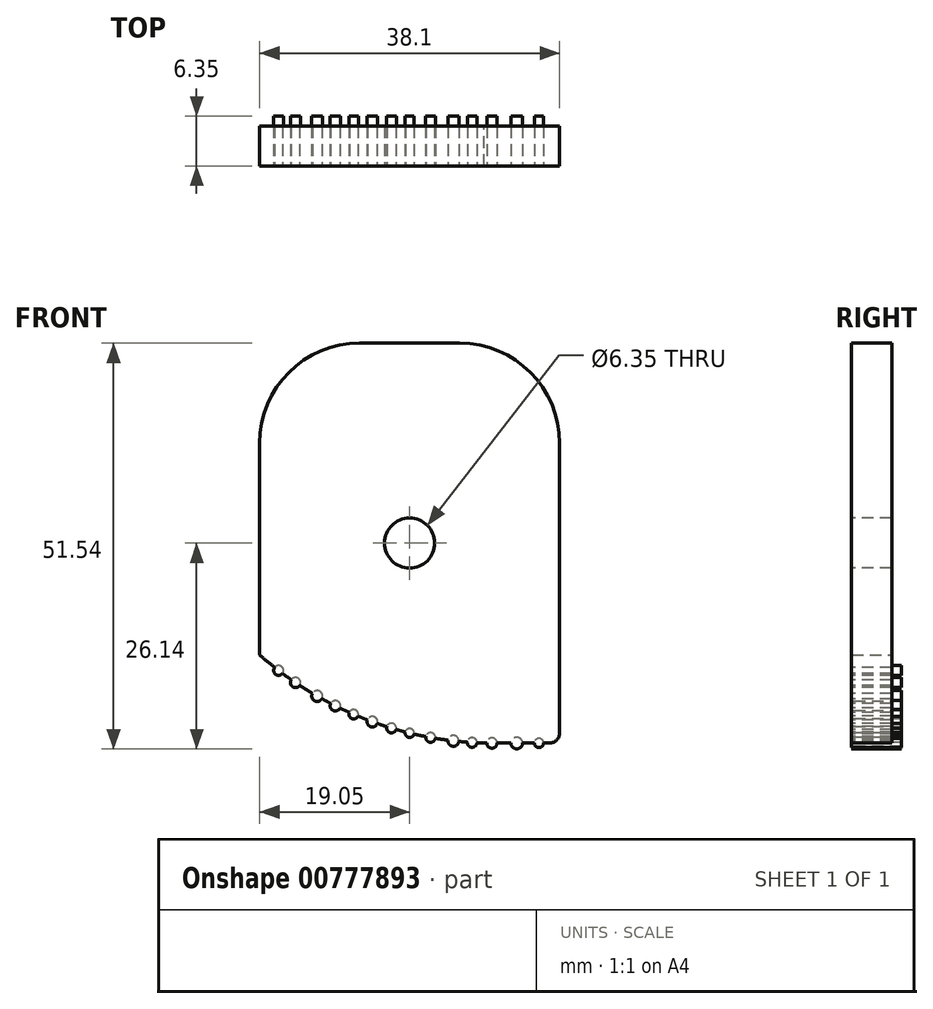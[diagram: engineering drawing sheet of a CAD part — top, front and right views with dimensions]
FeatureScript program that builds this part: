
annotation { "Feature Type Name" : "Feature", "Feature Type Description" : "" }
export const myFeature = defineFeature(function(context is Context, id is Id, definition is map)
    precondition{}
    {
        {
            var Q0;
            Q0=qCreatedBy(makeId("Front.planeOp"),FACE);
            var sketch = newSketch(context, id + "F0", { "sketchPlane" : qUnion([Q0])});
            skLineSegment(sketch, "E0.bottom", {"start": v(19.05, 25.4) * mm, "end": v(-19.05, 25.4) * mm});
            skLineSegment(sketch, "E0.top", {"start": v(19.05, -25.4) * mm, "end": v(-19.05, -25.4) * mm});
            skLineSegment(sketch, "E0.left", {"start": v(19.05, 25.4) * mm, "end": v(19.05, -25.4) * mm});
            skLineSegment(sketch, "E0.right", {"start": v(-19.05, 25.4) * mm, "end": v(-19.05, -25.4) * mm});
            skPoint(sketch, "E0.middle", {"position": v(0, 0) * mm});
            skArc(sketch, "E1", {"start": v(-19.05, -14.22) * mm, "mid": v(-5.78, -22.3) * mm, "end": v(9.44, -25.4) * mm});
            skSolve(sketch);
        }
        {
            var Q0;
            {var subQ1=sQuery(id+"F0.wireOp",EDGE,"E0.bottom");Q0=makeQuery(id+"F0.imprint","IMPRINT",FACE,{"disambiguationData":[TD([[makeQuery(id+"F0.imprint","IMPRINT",EDGE,{"derivedFrom":subQ1}),1.0]])]});}
            extrude(context, id + "F1", {"entities" : qUnion([Q0]), "depth" : 5.08 * mm, "offsetDistance" : 25.4 * mm});
        }
        {
            var Q0;
            Q0=makeQuery(id+"F1.opExtrude","CAP_FACE",FACE,{"disambiguationData":[OSD([sQuery(id+"F0.wireOp",EDGE,"E0.bottom"),sQuery(id+"F0.wireOp",EDGE,"E0.top"),sQuery(id+"F0.wireOp",EDGE,"E0.left"),sQuery(id+"F0.wireOp",EDGE,"E0.right"),sQuery(id+"F0.wireOp",EDGE,"E1")])],"isStart":false});
            var sketch = newSketch(context, id + "F2", { "sketchPlane" : qUnion([Q0])});
            skCircle(sketch, "E2", {"center": v(0, 0) * mm, "radius": 3.18 * mm});
            skSolve(sketch);
        }
        {
            var Q0;
            Q0 = qSketchRegion(id + "F2", true);
            extrude(context, id + "F3", {"entities" : qUnion([Q0]), "operationType" : NewBodyOperationType.REMOVE, "oppositeDirection" : true, "depth" : 25.4 * mm, "offsetDistance" : 25.4 * mm});
        }
        {
            var Q0;
            Q0=makeQuery(id+"F1.opExtrude","SWEPT_EDGE",EDGE,{"disambiguationData":[OSD([sQuery(id+"F0.wireOp",EDGE,"E0.bottom"),sQuery(id+"F0.wireOp",EDGE,"E0.left")])]});
            var Q1;
            Q1=makeQuery(id+"F1.opExtrude","SWEPT_EDGE",EDGE,{"disambiguationData":[OSD([sQuery(id+"F0.wireOp",EDGE,"E0.bottom"),sQuery(id+"F0.wireOp",EDGE,"E0.right")])]});
            fillet(context, id + "F4", {"entities" : qUnion([Q0, Q1]), "radius" : 12.7 * mm, "tangentPropagation" : true, "allowEdgeOverflow" : false});
        }
        {
            var Q0;
            Q0=makeQuery(id+"F1.opExtrude","SWEPT_EDGE",EDGE,{"disambiguationData":[OSD([sQuery(id+"F0.wireOp",EDGE,"E0.top"),sQuery(id+"F0.wireOp",EDGE,"E0.left")])]});
            fillet(context, id + "F5", {"entities" : qUnion([Q0]), "radius" : 1.27 * mm, "tangentPropagation" : true, "allowEdgeOverflow" : false});
        }
        {
            var Q0;
            Q0=makeQuery(id+"F1.opExtrude","CAP_FACE",FACE,{"disambiguationData":[OSD([sQuery(id+"F0.wireOp",EDGE,"E0.bottom"),sQuery(id+"F0.wireOp",EDGE,"E0.top"),sQuery(id+"F0.wireOp",EDGE,"E0.left"),sQuery(id+"F0.wireOp",EDGE,"E0.right"),sQuery(id+"F0.wireOp",EDGE,"E1")])],"isStart":false});
            var sketch = newSketch(context, id + "F6", { "sketchPlane" : qUnion([Q0])});
            skCircle(sketch, "E3", {"center": v(-16.65, -16.18) * mm, "radius": 0.62 * mm});
            skCircle(sketch, "E4", {"center": v(-14.5, -17.72) * mm, "radius": 0.64 * mm});
            skCircle(sketch, "E5", {"center": v(-11.75, -19.43) * mm, "radius": 0.7 * mm});
            skCircle(sketch, "E6", {"center": v(-9.44, -20.67) * mm, "radius": 0.66 * mm});
            skCircle(sketch, "E7", {"center": v(-7.11, -21.75) * mm, "radius": 0.6 * mm});
            skCircle(sketch, "E8", {"center": v(-4.74, -22.69) * mm, "radius": 0.67 * mm});
            skCircle(sketch, "E9", {"center": v(-2.3, -23.5) * mm, "radius": 0.61 * mm});
            skCircle(sketch, "E10", {"center": v(0, -24.13) * mm, "radius": 0.57 * mm});
            skCircle(sketch, "E11", {"center": v(2.66, -24.7) * mm, "radius": 0.61 * mm});
            skCircle(sketch, "E12", {"center": v(5.55, -25.12) * mm, "radius": 0.69 * mm});
            skCircle(sketch, "E13", {"center": v(7.93, -25.33) * mm, "radius": 0.62 * mm});
            skCircle(sketch, "E14", {"center": v(10.45, -25.4) * mm, "radius": 0.66 * mm});
            skCircle(sketch, "E15", {"center": v(13.6, -25.4) * mm, "radius": 0.74 * mm});
            skCircle(sketch, "E16", {"center": v(16.43, -25.4) * mm, "radius": 0.59 * mm});
            skSolve(sketch);
        }
        {
            var Q0;
            Q0 = qSketchRegion(id + "F6", true);
            extrude(context, id + "F7", {"entities" : qUnion([Q0]), "operationType" : NewBodyOperationType.ADD, "oppositeDirection" : true, "depth" : 6.35 * mm, "offsetDistance" : 25.4 * mm});
        }
    });
